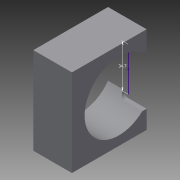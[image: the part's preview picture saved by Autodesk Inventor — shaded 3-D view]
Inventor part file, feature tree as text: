
AUTODESK INVENTOR PART (.ipt)
format: ipt  version: 2015 SP2 (Build 190223200, 223)  size: 115,712 bytes
history: native  units: mm
features: sketch x7, extrude x3, hole x3
ambient origin geometry x8: Origin, YZ Plane, XZ Plane, XY Plane, X Axis, Y Axis, Z Axis, Center Point
bodies: Solid1 (feature_tree)
feature tree (13):
  extrude  "Extrusion1"  Depth=31.0mm
  sketch  "Sketch2"  dims[d2=60.0mm d3=0.0mm d4=34.7mm]
  hole  "Hole1"  [1 undecoded]
  sketch  "Sketch4"  dims[d6=55.0mm d7=6.0mm d8=4.0mm d9=2.0mm d10=90.0deg d11=8.0mm d12=20.594885mm d13=8.0mm]
  sketch  "Sketch5"  dims[d14=8.0mm]
  hole  "Hole2"  [1 undecoded]
  hole  "Hole3"  [1 undecoded]
  extrude  "Extrusion2"  Depth=10.0mm TaperAngle=0.0deg
  extrude  "Extrusion3"  [1 undecoded]
  sketch  "Sketch1"  dims[d0=70.0mm d1=31.0mm]
  sketch  "Sketch3"  dims[d5=55.0mm]
  sketch  "Sketch6"  dims[d15=8.0mm d16=6.0mm d17=4.0mm d18=2.0mm d19=90.0deg d20=8.0mm d21=20.594885mm]
  sketch  "Sketch7"  dims[d22=8.0mm d23=6.0mm d24=4.0mm d25=2.0mm d26=90.0deg d27=8.0mm d28=20.594885mm d29=10.0mm d30=0.0mm d31=10.0mm d32=0.0mm]
note: 4 required parameter values undecoded (feature->parameter linkage not recoverable at this tier; creation-order binding heuristic only, values carry confidence <= 0.55)
